# Revit family: 4430FRK
name_source: partatom
category: Plumbing Fixtures
units: mm (PartAtom-declared; Revit-internal decimal feet)

## family parameters
Always vertical = Yes
Cut with Voids When Loaded = No
OmniClass Number = 23.45.00.00
OmniClass Title = Sanitary, Laundry, and Cleaning Equipment
Part Type = Normal
Room Calculation Point = No
Round Connector Dimension = Use Diameter
Shared = No
Work Plane-Based = No

## types (12) — shared parameters
Activation by = Mechanical Front Bubbler Button
Approx. Shipping Weight = 215 lbs.
Assembly Code = D2010800
BASIN_MATERIAL = Metal - Steel - Stainless - Chrome
BOTTLE_SHAPE MATERIAL = Metal - Steel - Stainless - Chrome
Bubbler Style = Vandal Resistant
CW Connection = Yes
Chilling Option = Non-refrigerated
DRAIN_MATERIAL = Metal - Steel - Stainless - Chrome
Description = Endura II Tubular Outdoor Fountain Tri-Level Pedestal Non-Filtered Non-Refrigerated
Dimensions (L x W x H) = 14Inch x 48Inch x 40 5/16Inch
Drain_Pipe 1 1/2" = 38 mm
HW Connection = No
Inlet_Pipe = 10 mm  [stored 0.0328084 ft]
Installation Location = Outdoor
Manufacturer = Elkay
Model = 4430FRK
Mounting Type = Floor Mount/Freestanding
No. of Stations Served = 3
PUSH_BUTTON_MATERIAL = Metal - Steel - Stainless - Chrome
Power = No Electrical Required
SINK_MATERIAL = Metal - Steel - Stainless - Chrome
URL = http://www.elkay.com
Vent Connection = No
Version = 1.0.0.0
Waste Connection = Yes
zero-valued in all types: Cost

## per-type parameters (varying)
| type | FOUNDATION_BODY_MATERIAL | Finish |
| Evergreen(EVG) | Evergreen (EVG) | Evergreen |
| Blue(BLU) | Blue (BLU) | Blue |
| Purple(PUR) | Purple (PUR) | Purple |
| Red(RED) | Red(RED) | Red |
| Terracotta(TER) | Terracotta(TER) | Terracotta |
| Orange(ORN) | Orange(ORN) | Orange |
| Yellow(YLW) | Yellow(YLW) | Yellow(YLW) |
| Black(BLK) | Black(BLK) | Black |
| Brown(BRN) | Brown(BRN) | Brown |
| Gray(GRY) | Grey(GRY) | Gray |
| Beige(BGE) | Beige(BGE) | Beige |
| White(WHT) | White(WHT) | White |

note: [stored X ft] marks values corroborated as IEEE doubles in the binary element streams (Revit-internal decimal feet)

## geometry (parser evidence)
native form markers: Sweep x26
no freeform markers — native parametric forms only
